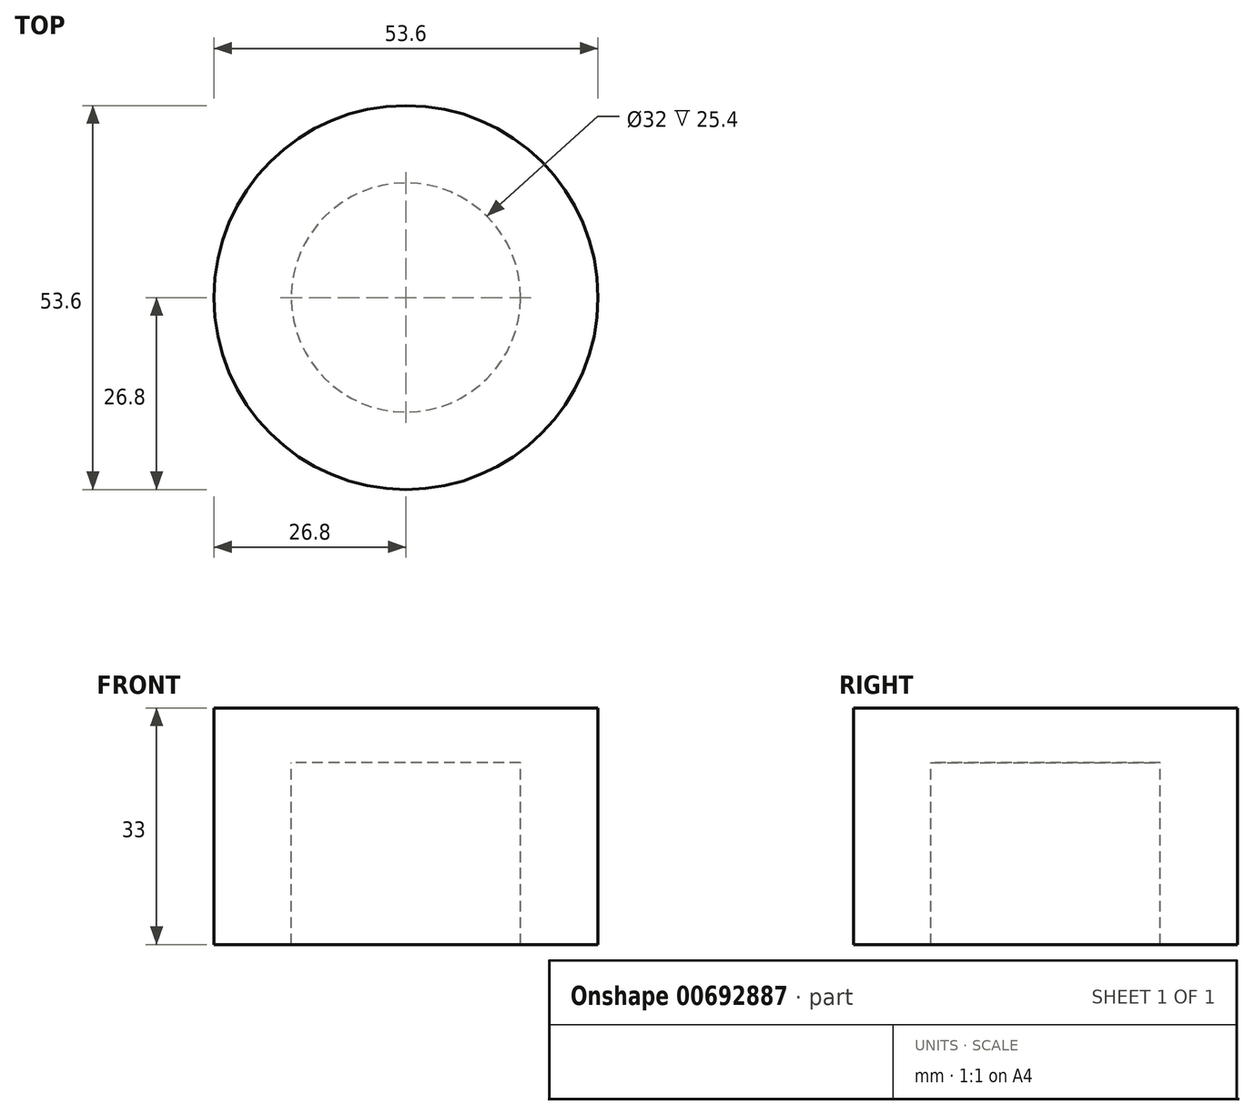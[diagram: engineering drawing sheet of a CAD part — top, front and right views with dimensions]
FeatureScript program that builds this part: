
annotation { "Feature Type Name" : "Feature", "Feature Type Description" : "" }
export const myFeature = defineFeature(function(context is Context, id is Id, definition is map)
    precondition{}
    {
        {
            var Q0;
            Q0=qCreatedBy(makeId("Front.planeOp"),FACE);
            var sketch = newSketch(context, id + "F0", { "sketchPlane" : qUnion([Q0])});
            skLineSegment(sketch, "E0", {"start": v(-26.8, 0) * mm, "end": v(-26.8, 33) * mm});
            skLineSegment(sketch, "E1", {"start": v(-26.8, 33) * mm, "end": v(0, 33) * mm});
            skLineSegment(sketch, "E2", {"start": v(0, 33) * mm, "end": v(0, 25.4) * mm});
            skLineSegment(sketch, "E3", {"start": v(0, 25.4) * mm, "end": v(-16, 25.4) * mm});
            skLineSegment(sketch, "E4", {"start": v(-16, 25.4) * mm, "end": v(-16, 0) * mm});
            skLineSegment(sketch, "E5", {"start": v(-16, 0) * mm, "end": v(-26.8, 0) * mm});
            skSolve(sketch);
        }
        {
            var Q0;
            Q0=qCreatedBy(makeId("Front.planeOp"),FACE);
            var sketch = newSketch(context, id + "F1", { "sketchPlane" : qUnion([Q0])});
            skLineSegment(sketch, "E6", {"start": v(0, 0) * mm, "end": v(0, -17.1) * mm});
            skSolve(sketch);
        }
        {
            var Q0;
            Q0 = qSketchRegion(id + "F0", true);
            var Q1;
            Q1=sQuery(id+"F1.wireOp",EDGE,"E6");
            revolve(context, id + "F2", {"entities" : qUnion([Q0]), "axis" : qUnion([Q1]), "revolveType" : RevolveType.FULL});
        }
    });
